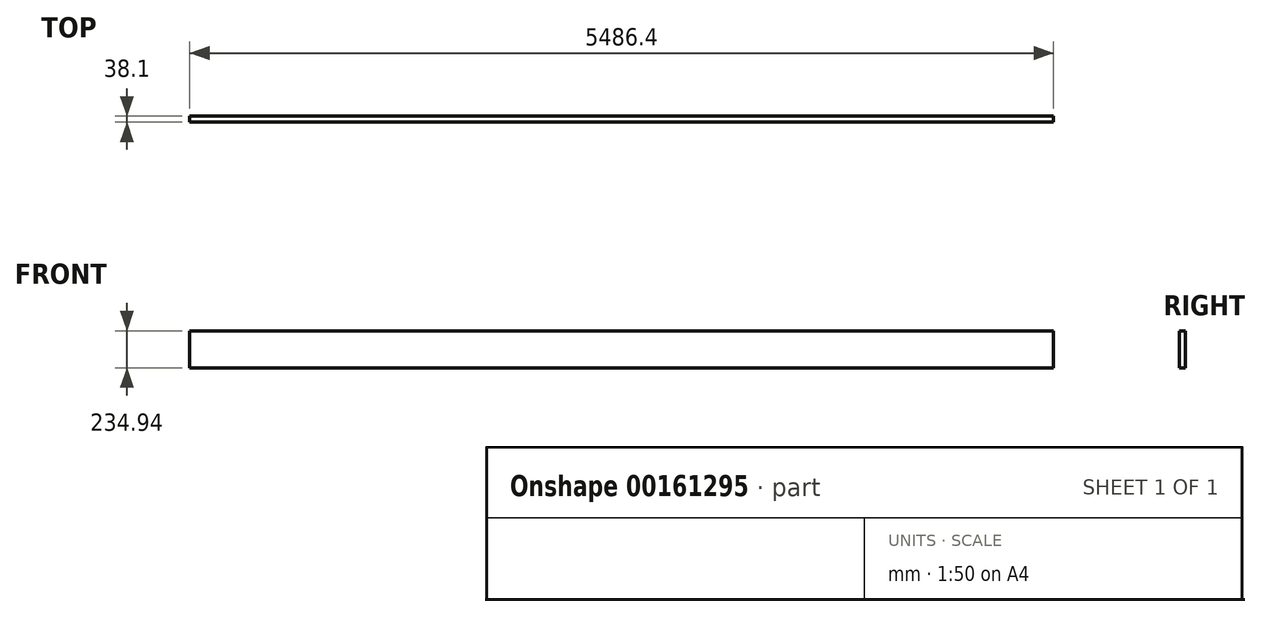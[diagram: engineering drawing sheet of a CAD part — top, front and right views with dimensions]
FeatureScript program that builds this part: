
annotation { "Feature Type Name" : "Feature", "Feature Type Description" : "" }
export const myFeature = defineFeature(function(context is Context, id is Id, definition is map)
    precondition{}
    {
        {
            var Q0;
            Q0=qCreatedBy(makeId("Top.planeOp"),FACE);
            var sketch = newSketch(context, id + "F0", { "sketchPlane" : qUnion([Q0])});
            skLineSegment(sketch, "E0.bottom", {"start": v(-2194.56, 38.1) * mm, "end": v(3291.84, 38.1) * mm});
            skLineSegment(sketch, "E0.top", {"start": v(-2194.56, 0) * mm, "end": v(3291.84, 0) * mm});
            skLineSegment(sketch, "E0.left", {"start": v(-2194.56, 38.1) * mm, "end": v(-2194.56, 0) * mm});
            skLineSegment(sketch, "E0.right", {"start": v(3291.84, 38.1) * mm, "end": v(3291.84, 0) * mm});
            skSolve(sketch);
        }
        {
            var Q0;
            Q0 = qSketchRegion(id + "F0", true);
            extrude(context, id + "F1", {"entities" : qUnion([Q0]), "depth" : 234.94 * mm});
        }
    });
